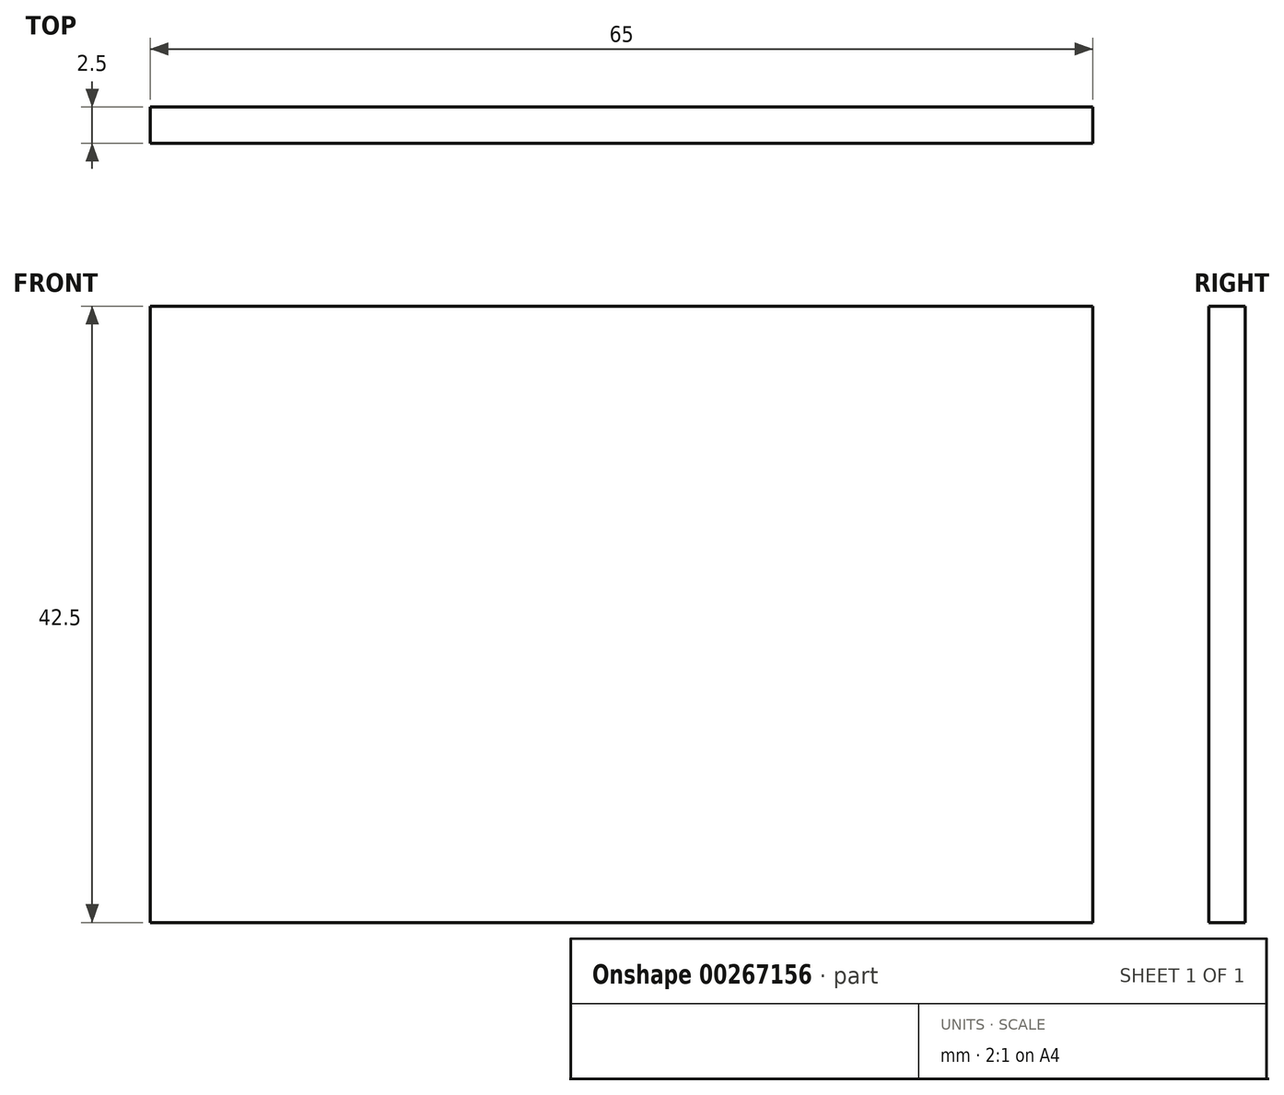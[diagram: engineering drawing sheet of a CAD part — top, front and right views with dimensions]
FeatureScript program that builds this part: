
annotation { "Feature Type Name" : "Feature", "Feature Type Description" : "" }
export const myFeature = defineFeature(function(context is Context, id is Id, definition is map)
    precondition{}
    {
        {
            var Q0;
            Q0=qCreatedBy(makeId("Top.planeOp"),FACE);
            var sketch = newSketch(context, id + "F0", { "sketchPlane" : qUnion([Q0])});
            skLineSegment(sketch, "E0.bottom", {"start": v(0, 0) * mm, "end": v(65, 0) * mm});
            skLineSegment(sketch, "E0.top", {"start": v(0, 2.5) * mm, "end": v(65, 2.5) * mm});
            skLineSegment(sketch, "E0.left", {"start": v(0, 0) * mm, "end": v(0, 2.5) * mm});
            skLineSegment(sketch, "E0.right", {"start": v(65, 0) * mm, "end": v(65, 2.5) * mm});
            skSolve(sketch);
        }
        {
            var Q0;
            Q0=makeQuery(id+"F0.imprint","IMPRINT",FACE,{"disambiguationData":[TD([[makeQuery(id+"F0.imprint","IMPRINT",EDGE,{"derivedFrom":sQuery(id+"F0.wireOp",EDGE,"E0.bottom")}),1.0]])]});
            extrude(context, id + "F1", {"entities" : qUnion([Q0]), "depth" : 42.5 * mm});
        }
    });
